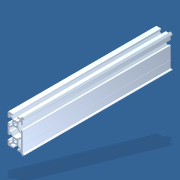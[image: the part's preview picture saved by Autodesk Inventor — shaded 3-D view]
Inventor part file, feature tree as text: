
AUTODESK INVENTOR PART (.ipt)
format: ipt  version: 2013 (Build 170138000, 138)  size: 452,608 bytes
history: native  units: in
note: dims shown in document units (in); Inventor stores cm internally (conversion verified against a paired STEP export)
features: other x1, imported_body x1, extrude x1, sketch x1
ambient origin geometry x8: Origin, YZ Plane, XZ Plane, XY Plane, X Axis, Y Axis, Z Axis, Center Point
feature tree (4):
  other  "MAKER_SLIDE_6_100"
  imported_body  "Base1"
  extrude  "Extrusion2"  [1 undecoded]
  sketch  "Sketch2"  dims[d2=3.937in d3=0.0in]
note: 1 required parameter value undecoded (feature->parameter linkage not recoverable at this tier; creation-order binding heuristic only, values carry confidence <= 0.55)
